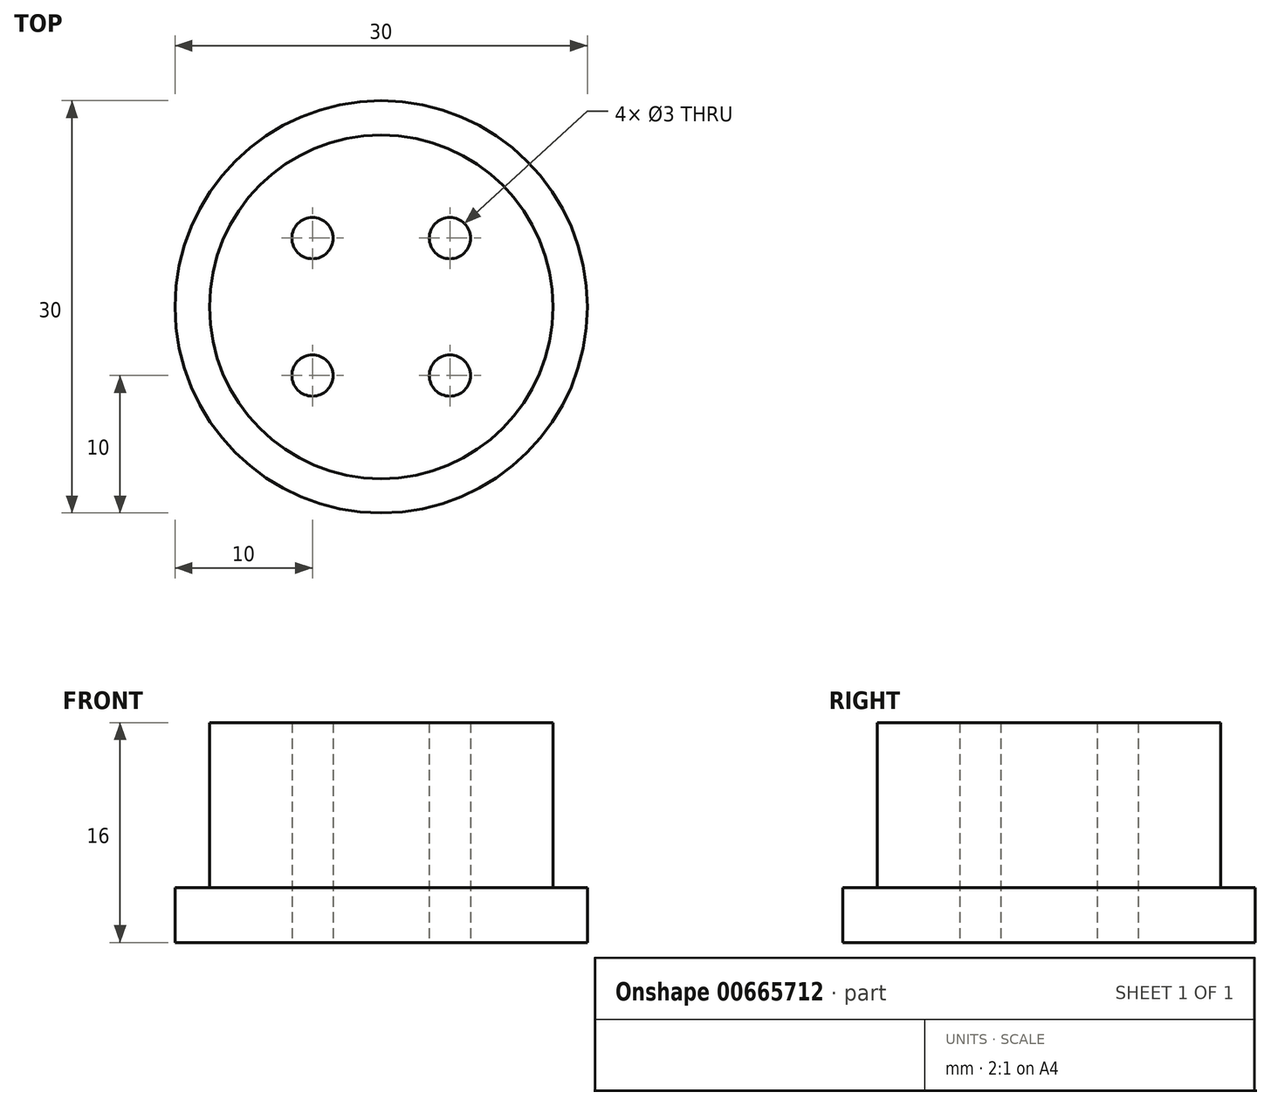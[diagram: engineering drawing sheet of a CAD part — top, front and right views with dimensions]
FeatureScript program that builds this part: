
annotation { "Feature Type Name" : "Feature", "Feature Type Description" : "" }
export const myFeature = defineFeature(function(context is Context, id is Id, definition is map)
    precondition{}
    {
        {
            var Q0;
            Q0=qCreatedBy(makeId("Top.planeOp"),FACE);
            var sketch = newSketch(context, id + "F0", { "sketchPlane" : qUnion([Q0])});
            skCircle(sketch, "E0", {"center": v(0, 0) * mm, "radius": 12.5 * mm});
            skCircle(sketch, "E1", {"center": v(0, 0) * mm, "radius": 23.5 * mm});
            skLineSegment(sketch, "E2.bottom", {"start": v(36.5, -36.5) * mm, "end": v(-36.5, -36.5) * mm});
            skLineSegment(sketch, "E2.top", {"start": v(36.5, 36.5) * mm, "end": v(-36.5, 36.5) * mm});
            skLineSegment(sketch, "E2.left", {"start": v(36.5, -36.5) * mm, "end": v(36.5, 36.5) * mm});
            skLineSegment(sketch, "E2.right", {"start": v(-36.5, -36.5) * mm, "end": v(-36.5, 36.5) * mm});
            skLineSegment(sketch, "E3.bottom", {"start": v(28.5, -28.5) * mm, "end": v(-28.5, -28.5) * mm});
            skLineSegment(sketch, "E3.top", {"start": v(28.5, 28.5) * mm, "end": v(-28.5, 28.5) * mm});
            skLineSegment(sketch, "E3.left", {"start": v(28.5, -28.5) * mm, "end": v(28.5, 28.5) * mm});
            skLineSegment(sketch, "E3.right", {"start": v(-28.5, -28.5) * mm, "end": v(-28.5, 28.5) * mm});
            skCircle(sketch, "E4", {"center": v(-28.5, 28.5) * mm, "radius": 3 * mm});
            skCircle(sketch, "E5", {"center": v(28.5, 28.5) * mm, "radius": 3 * mm});
            skCircle(sketch, "E6", {"center": v(28.5, -28.5) * mm, "radius": 3 * mm});
            skCircle(sketch, "E7", {"center": v(-28.5, -28.5) * mm, "radius": 3 * mm});
            skCircle(sketch, "E8", {"center": v(0, 0) * mm, "radius": 17.5 * mm});
            skCircle(sketch, "E9", {"center": v(0, 0) * mm, "radius": 15 * mm});
            skCircle(sketch, "E10", {"center": v(-28.5, 28.5) * mm, "radius": 8 * mm});
            skCircle(sketch, "E11", {"center": v(28.5, 28.5) * mm, "radius": 8 * mm});
            skCircle(sketch, "E12", {"center": v(28.5, -28.5) * mm, "radius": 8 * mm});
            skCircle(sketch, "E13", {"center": v(-28.5, -28.5) * mm, "radius": 8 * mm});
            skLineSegment(sketch, "E14.bottom", {"start": v(5, -5) * mm, "end": v(-5, -5) * mm});
            skLineSegment(sketch, "E14.top", {"start": v(5, 5) * mm, "end": v(-5, 5) * mm});
            skLineSegment(sketch, "E14.left", {"start": v(5, -5) * mm, "end": v(5, 5) * mm});
            skLineSegment(sketch, "E14.right", {"start": v(-5, -5) * mm, "end": v(-5, 5) * mm});
            skCircle(sketch, "E15", {"center": v(-5, 5) * mm, "radius": 1.5 * mm});
            skCircle(sketch, "E16", {"center": v(5, 5) * mm, "radius": 1.5 * mm});
            skCircle(sketch, "E17", {"center": v(5, -5) * mm, "radius": 1.5 * mm});
            skCircle(sketch, "E18", {"center": v(-5, -5) * mm, "radius": 1.5 * mm});
            skSolve(sketch);
        }
        {
            var Q0;
            Q0=makeQuery(id+"F0.imprint","IMPRINT",FACE,{"disambiguationData":[TD([[makeQuery(id+"F0.imprint","IMPRINT",EDGE,{"derivedFrom":sQuery(id+"F0.wireOp",EDGE,"E0")}),1.0]])]});
            var Q1;
            {var subQ5=sQuery(id+"F0.wireOp",EDGE,"E17");var subQ10=sQuery(id+"F0.wireOp",EDGE,"E14.bottom");var subQ15=makeQuery(id+"F0.imprint","INTERSECT",VERTEX,{"derivedFrom":[subQ10,subQ5]});Q1=makeQuery(id+"F0.imprint","IMPRINT",FACE,{"disambiguationData":[TD([[makeQuery(id+"F0.imprint","IMPRINT",EDGE,{"disambiguationData":[TD([[subQ15,-1.0]])],"derivedFrom":subQ10}),-1.0]])]});}
            extrude(context, id + "F1", {"entities" : qUnion([Q0, Q1]), "depth" : 16 * mm, "offsetDistance" : 25 * mm});
        }
        {
            var Q0;
            Q0=makeQuery(id+"F0.imprint","IMPRINT",FACE,{"disambiguationData":[TD([[makeQuery(id+"F0.imprint","IMPRINT",EDGE,{"derivedFrom":sQuery(id+"F0.wireOp",EDGE,"E0")}),-1.0]])]});
            extrude(context, id + "F2", {"entities" : qUnion([Q0]), "operationType" : NewBodyOperationType.ADD, "depth" : 4 * mm, "offsetDistance" : 25 * mm});
        }
    });
